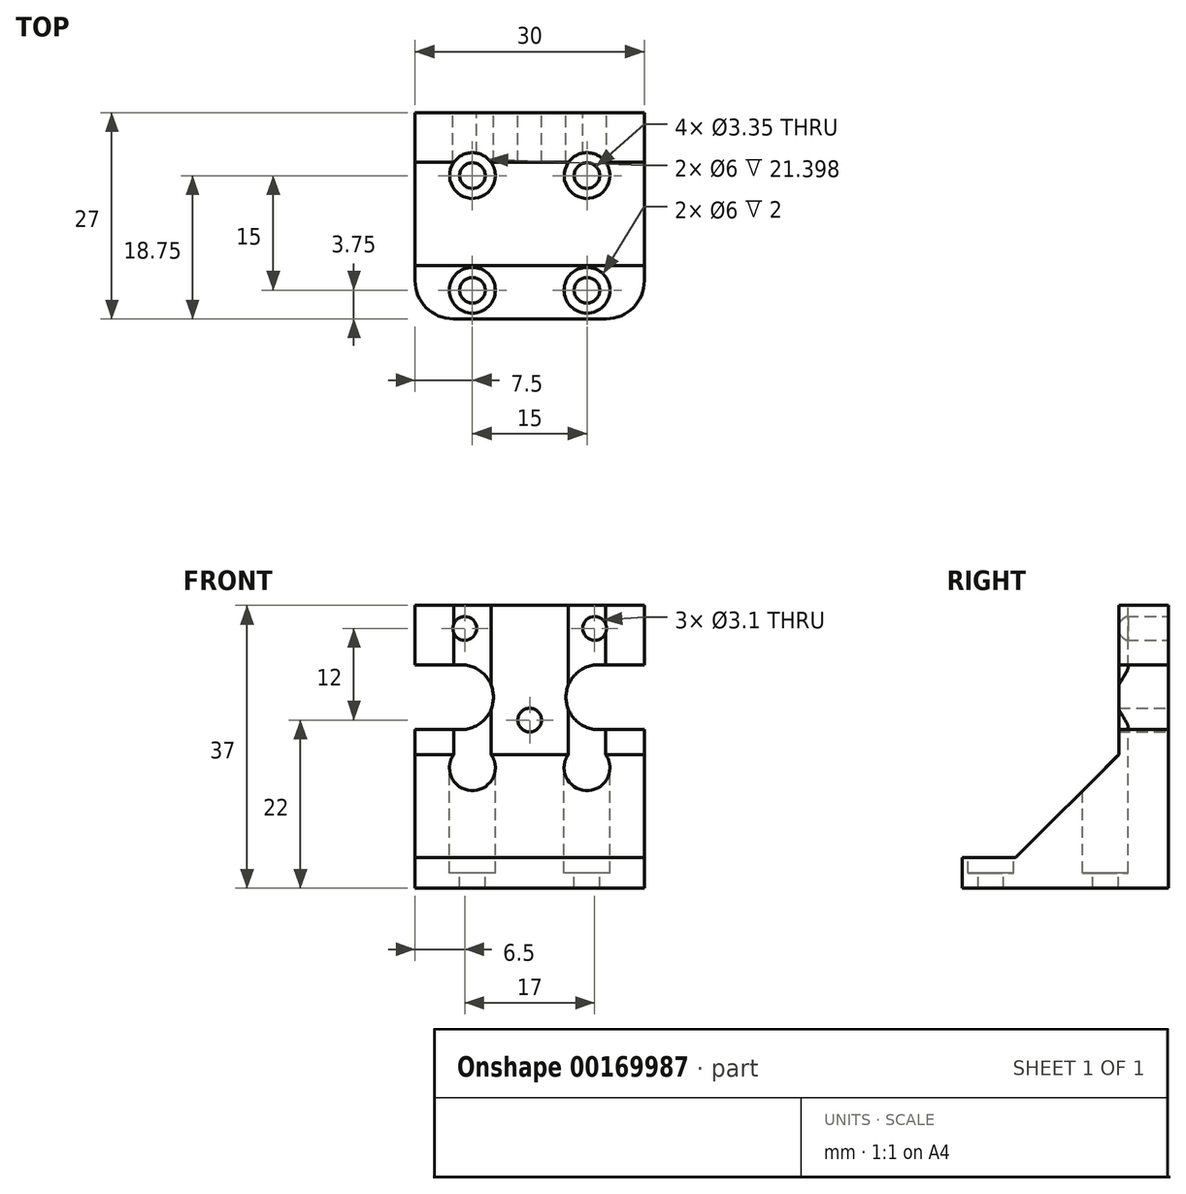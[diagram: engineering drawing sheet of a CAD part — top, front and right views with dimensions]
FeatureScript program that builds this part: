
annotation { "Feature Type Name" : "Feature", "Feature Type Description" : "" }
export const myFeature = defineFeature(function(context is Context, id is Id, definition is map)
    precondition{}
    {
        {
            var Q0;
            Q0=qCreatedBy(makeId("Top.planeOp"),FACE);
            var sketch = newSketch(context, id + "F0", { "sketchPlane" : qUnion([Q0])});
            skLineSegment(sketch, "E0.bottom", {"start": v(0, 0) * mm, "end": v(30, 0) * mm});
            skLineSegment(sketch, "E0.top", {"start": v(0, 22.5) * mm, "end": v(30, 22.5) * mm});
            skLineSegment(sketch, "E0.left", {"start": v(0, 0) * mm, "end": v(0, 22.5) * mm});
            skLineSegment(sketch, "E0.right", {"start": v(30, 0) * mm, "end": v(30, 22.5) * mm});
            skLineSegment(sketch, "E1.bottom", {"start": v(0, 27) * mm, "end": v(30, 27) * mm});
            skLineSegment(sketch, "E1.top", {"start": v(0, 20.5) * mm, "end": v(30, 20.5) * mm});
            skLineSegment(sketch, "E1.left", {"start": v(0, 27) * mm, "end": v(0, 20.5) * mm});
            skLineSegment(sketch, "E1.right", {"start": v(30, 27) * mm, "end": v(30, 20.5) * mm});
            skSolve(sketch);
        }
        {
            var Q0;
            Q0=makeQuery(id+"F0.imprint","IMPRINT",FACE,{"disambiguationData":[TD([[makeQuery(id+"F0.imprint","IMPRINT",EDGE,{"derivedFrom":sQuery(id+"F0.wireOp",EDGE,"E0.bottom")}),1.0]])]});
            var Q1;
            {var subQ0=sQuery(id+"F0.wireOp",EDGE,"E0.top");Q1=makeQuery(id+"F0.imprint","IMPRINT",FACE,{"disambiguationData":[TD([[makeQuery(id+"F0.imprint","IMPRINT",EDGE,{"derivedFrom":subQ0}),-1.0]])]});}
            extrude(context, id + "F1", {"entities" : qUnion([Q0, Q1]), "depth" : 4 * mm});
        }
        {
            var Q0;
            Q0=makeQuery(id+"F0.imprint","IMPRINT",FACE,{"disambiguationData":[TD([[makeQuery(id+"F0.imprint","IMPRINT",EDGE,{"derivedFrom":sQuery(id+"F0.wireOp",EDGE,"E0.top")}),1.0]])]});
            var Q1;
            {var subQ0=sQuery(id+"F0.wireOp",EDGE,"E0.top");Q1=makeQuery(id+"F0.imprint","IMPRINT",FACE,{"disambiguationData":[TD([[makeQuery(id+"F0.imprint","IMPRINT",EDGE,{"derivedFrom":subQ0}),-1.0]])]});}
            extrude(context, id + "F2", {"entities" : qUnion([Q0, Q1]), "operationType" : NewBodyOperationType.ADD, "depth" : 37 * mm});
        }
        {
            var Q0;
            Q0=makeQuery(id+"F1.opExtrude","CAP_FACE",FACE,{"disambiguationData":[OSD([sQuery(id+"F0.wireOp",EDGE,"E0.bottom"),sQuery(id+"F0.wireOp",EDGE,"E0.top"),sQuery(id+"F0.wireOp",EDGE,"E0.left"),sQuery(id+"F0.wireOp",EDGE,"E0.right")])],"isStart":false});
            var sketch = newSketch(context, id + "F3", { "sketchPlane" : qUnion([Q0])});
            skCircle(sketch, "E2", {"center": v(7.5, 18.75) * mm, "radius": 1.68 * mm});
            skCircle(sketch, "E3", {"center": v(22.5, 18.75) * mm, "radius": 1.68 * mm});
            skCircle(sketch, "E4", {"center": v(7.5, 3.75) * mm, "radius": 1.68 * mm});
            skCircle(sketch, "E5", {"center": v(22.5, 3.75) * mm, "radius": 1.68 * mm});
            skLineSegment(sketch, "E6", {"start": v(22.5, 3.75) * mm, "end": v(30, 3.75) * mm});
            skCircle(sketch, "E7", {"center": v(7.5, 18.75) * mm, "radius": 3 * mm});
            skCircle(sketch, "E8", {"center": v(22.5, 18.75) * mm, "radius": 3 * mm});
            skCircle(sketch, "E9", {"center": v(7.5, 3.75) * mm, "radius": 3 * mm});
            skCircle(sketch, "E10", {"center": v(22.5, 3.75) * mm, "radius": 3 * mm});
            skSolve(sketch);
        }
        {
            var Q0;
            Q0=makeQuery(id+"F3.imprint","IMPRINT",FACE,{"disambiguationData":[TD([[makeQuery(id+"F3.imprint","IMPRINT",EDGE,{"derivedFrom":sQuery(id+"F3.wireOp",EDGE,"E2")}),1.0]])]});
            var Q1;
            Q1=makeQuery(id+"F3.imprint","IMPRINT",FACE,{"disambiguationData":[TD([[makeQuery(id+"F3.imprint","IMPRINT",EDGE,{"derivedFrom":sQuery(id+"F3.wireOp",EDGE,"E3")}),1.0]])]});
            var Q2;
            Q2=makeQuery(id+"F3.imprint","IMPRINT",FACE,{"disambiguationData":[TD([[makeQuery(id+"F3.imprint","IMPRINT",EDGE,{"derivedFrom":sQuery(id+"F3.wireOp",EDGE,"E5")}),1.0]])]});
            var Q3;
            Q3=makeQuery(id+"F3.imprint","IMPRINT",FACE,{"disambiguationData":[TD([[makeQuery(id+"F3.imprint","IMPRINT",EDGE,{"derivedFrom":sQuery(id+"F3.wireOp",EDGE,"E4")}),1.0]])]});
            extrude(context, id + "F4", {"entities" : qUnion([Q0, Q1, Q2, Q3]), "operationType" : NewBodyOperationType.REMOVE, "oppositeDirection" : true, "depth" : 25 * mm});
        }
        {
            var Q0;
            Q0=makeQuery(id+"F3.imprint","IMPRINT",FACE,{"disambiguationData":[TD([[makeQuery(id+"F3.imprint","IMPRINT",EDGE,{"derivedFrom":sQuery(id+"F3.wireOp",EDGE,"E2")}),-1.0]])]});
            var Q1;
            Q1=makeQuery(id+"F3.imprint","IMPRINT",FACE,{"disambiguationData":[TD([[makeQuery(id+"F3.imprint","IMPRINT",EDGE,{"derivedFrom":sQuery(id+"F3.wireOp",EDGE,"E3")}),-1.0]])]});
            var Q2;
            Q2=makeQuery(id+"F3.imprint","IMPRINT",FACE,{"disambiguationData":[TD([[makeQuery(id+"F3.imprint","IMPRINT",EDGE,{"derivedFrom":sQuery(id+"F3.wireOp",EDGE,"E5")}),-1.0]])]});
            var Q3;
            Q3=makeQuery(id+"F3.imprint","IMPRINT",FACE,{"disambiguationData":[TD([[makeQuery(id+"F3.imprint","IMPRINT",EDGE,{"derivedFrom":sQuery(id+"F3.wireOp",EDGE,"E4")}),-1.0]])]});
            var Q4;
            {var subQ0=sQuery(id+"F3.wireOp",EDGE,"E7");var subQ1=makeQuery(id+"F2.boolean.opBoolean","INTERSECT",EDGE,{"derivedFrom":[makeQuery(id+"F1.opExtrude","CAP_FACE",FACE,{"disambiguationData":[OSD([sQuery(id+"F0.wireOp",EDGE,"E0.bottom"),sQuery(id+"F0.wireOp",EDGE,"E0.left"),sQuery(id+"F0.wireOp",EDGE,"E0.right"),sQuery(id+"F0.wireOp",EDGE,"E0.top"),sQuery(id+"F0.wireOp",EDGE,"E1.left"),sQuery(id+"F0.wireOp",EDGE,"E1.right")])],"isStart":false}),makeQuery(id+"F2.opExtrude","SWEPT_FACE",FACE,{"disambiguationData":[OSD([sQuery(id+"F0.wireOp",EDGE,"E1.top")])]})]});var subQ2=makeQuery(id+"F3.imprint","INTERSECT",VERTEX,{"disambiguationData":[OD(0.0)],"derivedFrom":[subQ1,subQ0]});Q4=makeQuery(id+"F3.imprint","IMPRINT",FACE,{"disambiguationData":[TD([[makeQuery(id+"F3.imprint","IMPRINT",EDGE,{"disambiguationData":[TD([[subQ2,1.0]])],"derivedFrom":subQ0}),1.0]])]});}
            var Q5;
            {var subQ0=sQuery(id+"F3.wireOp",EDGE,"E8");var subQ1=makeQuery(id+"F2.boolean.opBoolean","INTERSECT",EDGE,{"derivedFrom":[makeQuery(id+"F1.opExtrude","CAP_FACE",FACE,{"disambiguationData":[OSD([sQuery(id+"F0.wireOp",EDGE,"E0.bottom"),sQuery(id+"F0.wireOp",EDGE,"E0.left"),sQuery(id+"F0.wireOp",EDGE,"E0.right"),sQuery(id+"F0.wireOp",EDGE,"E0.top"),sQuery(id+"F0.wireOp",EDGE,"E1.left"),sQuery(id+"F0.wireOp",EDGE,"E1.right")])],"isStart":false}),makeQuery(id+"F2.opExtrude","SWEPT_FACE",FACE,{"disambiguationData":[OSD([sQuery(id+"F0.wireOp",EDGE,"E1.top")])]})]});var subQ2=makeQuery(id+"F3.imprint","INTERSECT",VERTEX,{"disambiguationData":[OD(0.0)],"derivedFrom":[subQ1,subQ0]});Q5=makeQuery(id+"F3.imprint","IMPRINT",FACE,{"disambiguationData":[TD([[makeQuery(id+"F3.imprint","IMPRINT",EDGE,{"disambiguationData":[TD([[subQ2,-1.0]])],"derivedFrom":subQ0}),1.0]])]});}
            extrude(context, id + "F5", {"entities" : qUnion([Q0, Q1, Q2, Q3, Q4, Q5]), "operationType" : NewBodyOperationType.REMOVE, "oppositeDirection" : true, "depth" : 2 * mm});
        }
        {
            var Q0;
            {var subQ0=sQuery(id+"F3.wireOp",EDGE,"E7");var subQ1=makeQuery(id+"F2.boolean.opBoolean","INTERSECT",EDGE,{"derivedFrom":[makeQuery(id+"F1.opExtrude","CAP_FACE",FACE,{"disambiguationData":[OSD([sQuery(id+"F0.wireOp",EDGE,"E0.bottom"),sQuery(id+"F0.wireOp",EDGE,"E0.left"),sQuery(id+"F0.wireOp",EDGE,"E0.right"),sQuery(id+"F0.wireOp",EDGE,"E0.top"),sQuery(id+"F0.wireOp",EDGE,"E1.left"),sQuery(id+"F0.wireOp",EDGE,"E1.right")])],"isStart":false}),makeQuery(id+"F2.opExtrude","SWEPT_FACE",FACE,{"disambiguationData":[OSD([sQuery(id+"F0.wireOp",EDGE,"E1.top")])]})]});var subQ2=makeQuery(id+"F3.imprint","INTERSECT",VERTEX,{"disambiguationData":[OD(0.0)],"derivedFrom":[subQ1,subQ0]});Q0=makeQuery(id+"F3.imprint","IMPRINT",FACE,{"disambiguationData":[TD([[makeQuery(id+"F3.imprint","IMPRINT",EDGE,{"disambiguationData":[TD([[subQ2,1.0]])],"derivedFrom":subQ0}),1.0]])]});}
            var Q1;
            Q1=makeQuery(id+"F3.imprint","IMPRINT",FACE,{"disambiguationData":[TD([[makeQuery(id+"F3.imprint","IMPRINT",EDGE,{"derivedFrom":sQuery(id+"F3.wireOp",EDGE,"E2")}),-1.0]])]});
            var Q2;
            {var subQ0=sQuery(id+"F3.wireOp",EDGE,"E8");var subQ1=makeQuery(id+"F2.boolean.opBoolean","INTERSECT",EDGE,{"derivedFrom":[makeQuery(id+"F1.opExtrude","CAP_FACE",FACE,{"disambiguationData":[OSD([sQuery(id+"F0.wireOp",EDGE,"E0.bottom"),sQuery(id+"F0.wireOp",EDGE,"E0.left"),sQuery(id+"F0.wireOp",EDGE,"E0.right"),sQuery(id+"F0.wireOp",EDGE,"E0.top"),sQuery(id+"F0.wireOp",EDGE,"E1.left"),sQuery(id+"F0.wireOp",EDGE,"E1.right")])],"isStart":false}),makeQuery(id+"F2.opExtrude","SWEPT_FACE",FACE,{"disambiguationData":[OSD([sQuery(id+"F0.wireOp",EDGE,"E1.top")])]})]});var subQ2=makeQuery(id+"F3.imprint","INTERSECT",VERTEX,{"disambiguationData":[OD(0.0)],"derivedFrom":[subQ1,subQ0]});Q2=makeQuery(id+"F3.imprint","IMPRINT",FACE,{"disambiguationData":[TD([[makeQuery(id+"F3.imprint","IMPRINT",EDGE,{"disambiguationData":[TD([[subQ2,-1.0]])],"derivedFrom":subQ0}),1.0]])]});}
            var Q3;
            Q3=makeQuery(id+"F3.imprint","IMPRINT",FACE,{"disambiguationData":[TD([[makeQuery(id+"F3.imprint","IMPRINT",EDGE,{"derivedFrom":sQuery(id+"F3.wireOp",EDGE,"E3")}),-1.0]])]});
            var Q4;
            Q4=makeQuery(id+"F2.opExtrude","CAP_FACE",FACE,{"disambiguationData":[OSD([sQuery(id+"F0.wireOp",EDGE,"E1.bottom"),sQuery(id+"F0.wireOp",EDGE,"E1.top"),sQuery(id+"F0.wireOp",EDGE,"E1.left"),sQuery(id+"F0.wireOp",EDGE,"E1.right")])],"isStart":false});
            extrude(context, id + "F6", {"entities" : qUnion([Q0, Q1, Q2, Q3]), "operationType" : NewBodyOperationType.REMOVE, "endBound" : BoundingType.UP_TO_SURFACE, "endBoundEntityFace" : qUnion([Q4]), "depth" : 25 * mm});
        }
        {
            var Q0;
            Q0=makeQuery(id+"F1.opExtrude","SWEPT_EDGE",EDGE,{"disambiguationData":[OSD([sQuery(id+"F0.wireOp",EDGE,"E0.bottom"),sQuery(id+"F0.wireOp",EDGE,"E0.left")])]});
            var Q1;
            Q1=makeQuery(id+"F1.opExtrude","SWEPT_EDGE",EDGE,{"disambiguationData":[OSD([sQuery(id+"F0.wireOp",EDGE,"E0.bottom"),sQuery(id+"F0.wireOp",EDGE,"E0.right")])]});
            var Q2;
            Q2=makeQuery(id+"F1.opExtrude","SWEPT_EDGE",EDGE,{"disambiguationData":[OSD([sQuery(id+"F0.wireOp",EDGE,"E0.top"),sQuery(id+"F0.wireOp",EDGE,"E0.right")])]});
            var Q3;
            Q3=makeQuery(id+"F1.opExtrude","SWEPT_EDGE",EDGE,{"disambiguationData":[OSD([sQuery(id+"F0.wireOp",EDGE,"E0.top"),sQuery(id+"F0.wireOp",EDGE,"E0.left")])]});
            fillet(context, id + "F7", {"entities" : qUnion([Q0, Q1, Q2, Q3]), "radius" : 5 * mm, "tangentPropagation" : true, "allowEdgeOverflow" : false});
        }
        {
            var Q0;
            Q0=makeQuery(id+"F2.opExtrude","SWEPT_FACE",FACE,{"disambiguationData":[OSD([sQuery(id+"F0.wireOp",EDGE,"E1.bottom")])]});
            var sketch = newSketch(context, id + "F8", { "sketchPlane" : qUnion([Q0])});
            skCircle(sketch, "E11", {"center": v(-23.5, 34) * mm, "radius": 1.55 * mm});
            skCircle(sketch, "E12", {"center": v(-6.5, 34) * mm, "radius": 1.55 * mm});
            skCircle(sketch, "E13", {"center": v(-15, 22) * mm, "radius": 1.55 * mm});
            skCircle(sketch, "E14", {"center": v(-24, 25) * mm, "radius": 4.25 * mm});
            skCircle(sketch, "E15", {"center": v(-6, 25) * mm, "radius": 4.25 * mm});
            skSolve(sketch);
        }
        {
            var Q0;
            Q0=makeQuery(id+"F8.imprint","IMPRINT",FACE,{"disambiguationData":[TD([[makeQuery(id+"F8.imprint","IMPRINT",EDGE,{"derivedFrom":sQuery(id+"F8.wireOp",EDGE,"E14")}),1.0]])]});
            var Q1;
            Q1=makeQuery(id+"F8.imprint","IMPRINT",FACE,{"disambiguationData":[TD([[makeQuery(id+"F8.imprint","IMPRINT",EDGE,{"derivedFrom":sQuery(id+"F8.wireOp",EDGE,"E11")}),1.0]])]});
            var Q2;
            Q2=makeQuery(id+"F8.imprint","IMPRINT",FACE,{"disambiguationData":[TD([[makeQuery(id+"F8.imprint","IMPRINT",EDGE,{"derivedFrom":sQuery(id+"F8.wireOp",EDGE,"E12")}),1.0]])]});
            var Q3;
            Q3=makeQuery(id+"F8.imprint","IMPRINT",FACE,{"disambiguationData":[TD([[makeQuery(id+"F8.imprint","IMPRINT",EDGE,{"derivedFrom":sQuery(id+"F8.wireOp",EDGE,"E15")}),1.0]])]});
            var Q4;
            Q4=makeQuery(id+"F8.imprint","IMPRINT",FACE,{"disambiguationData":[TD([[makeQuery(id+"F8.imprint","IMPRINT",EDGE,{"derivedFrom":sQuery(id+"F8.wireOp",EDGE,"E13")}),1.0]])]});
            extrude(context, id + "F9", {"entities" : qUnion([Q0, Q1, Q2, Q3, Q4]), "operationType" : NewBodyOperationType.REMOVE, "oppositeDirection" : true, "depth" : 7 * mm});
        }
        {
            var Q0;
            {var subQ0=sQuery(id+"F0.wireOp",EDGE,"E1.left");var subQ1=sQuery(id+"F3.wireOp",EDGE,"E7");var subQ2=makeQuery(id+"F2.opExtrude","SWEPT_FACE",FACE,{"disambiguationData":[OSD([sQuery(id+"F0.wireOp",EDGE,"E1.top")])]});var subQ3=sQuery(id+"F0.wireOp",EDGE,"E0.left");var subQ4=makeQuery(id+"F1.opExtrude","CAP_FACE",FACE,{"disambiguationData":[OSD([sQuery(id+"F0.wireOp",EDGE,"E0.bottom"),subQ3,sQuery(id+"F0.wireOp",EDGE,"E0.right"),sQuery(id+"F0.wireOp",EDGE,"E0.top"),subQ0,sQuery(id+"F0.wireOp",EDGE,"E1.right")])],"isStart":false});Q0=makeQuery(id+"F5.boolean.opBoolean","SPLIT",EDGE,{"disambiguationData":[TD([subQ4,makeQuery(id+"F1.opExtrude","SWEPT_FACE",FACE,{"disambiguationData":[OSD([subQ3,subQ0])]}),subQ2,makeQuery(id+"F2.opExtrude","SWEPT_FACE",FACE,{"disambiguationData":[OSD([subQ0])]}),makeQuery(id+"F5.opExtrude","CAP_FACE",FACE,{"disambiguationData":[OSD([sQuery(id+"F3.wireOp",EDGE,"E2"),subQ1])],"isStart":true}),makeQuery(id+"F5.opExtrude","SWEPT_FACE",FACE,{"disambiguationData":[OSD([subQ1])]})])],"derivedFrom":makeQuery(id+"F2.boolean.opBoolean","INTERSECT",EDGE,{"derivedFrom":[subQ4,subQ2]})});}
            var Q1;
            {var subQ0=sQuery(id+"F3.wireOp",EDGE,"E8");var subQ1=sQuery(id+"F3.wireOp",EDGE,"E7");var subQ2=makeQuery(id+"F2.opExtrude","SWEPT_FACE",FACE,{"disambiguationData":[OSD([sQuery(id+"F0.wireOp",EDGE,"E1.top")])]});var subQ3=makeQuery(id+"F1.opExtrude","CAP_FACE",FACE,{"disambiguationData":[OSD([sQuery(id+"F0.wireOp",EDGE,"E0.bottom"),sQuery(id+"F0.wireOp",EDGE,"E0.left"),sQuery(id+"F0.wireOp",EDGE,"E0.right"),sQuery(id+"F0.wireOp",EDGE,"E0.top"),sQuery(id+"F0.wireOp",EDGE,"E1.left"),sQuery(id+"F0.wireOp",EDGE,"E1.right")])],"isStart":false});Q1=makeQuery(id+"F5.boolean.opBoolean","SPLIT",EDGE,{"disambiguationData":[TD([subQ3,subQ2,makeQuery(id+"F5.opExtrude","CAP_FACE",FACE,{"disambiguationData":[OSD([sQuery(id+"F3.wireOp",EDGE,"E2"),subQ1])],"isStart":true}),makeQuery(id+"F5.opExtrude","CAP_FACE",FACE,{"disambiguationData":[OSD([sQuery(id+"F3.wireOp",EDGE,"E3"),subQ0])],"isStart":true}),makeQuery(id+"F5.opExtrude","SWEPT_FACE",FACE,{"disambiguationData":[OSD([subQ1])]}),makeQuery(id+"F5.opExtrude","SWEPT_FACE",FACE,{"disambiguationData":[OSD([subQ0])]})])],"derivedFrom":makeQuery(id+"F2.boolean.opBoolean","INTERSECT",EDGE,{"derivedFrom":[subQ3,subQ2]})});}
            var Q2;
            {var subQ0=sQuery(id+"F0.wireOp",EDGE,"E1.right");var subQ1=sQuery(id+"F3.wireOp",EDGE,"E8");var subQ2=makeQuery(id+"F2.opExtrude","SWEPT_FACE",FACE,{"disambiguationData":[OSD([sQuery(id+"F0.wireOp",EDGE,"E1.top")])]});var subQ3=sQuery(id+"F0.wireOp",EDGE,"E0.right");var subQ4=makeQuery(id+"F1.opExtrude","CAP_FACE",FACE,{"disambiguationData":[OSD([sQuery(id+"F0.wireOp",EDGE,"E0.bottom"),sQuery(id+"F0.wireOp",EDGE,"E0.left"),subQ3,sQuery(id+"F0.wireOp",EDGE,"E0.top"),sQuery(id+"F0.wireOp",EDGE,"E1.left"),subQ0])],"isStart":false});Q2=makeQuery(id+"F5.boolean.opBoolean","SPLIT",EDGE,{"disambiguationData":[TD([subQ4,makeQuery(id+"F1.opExtrude","SWEPT_FACE",FACE,{"disambiguationData":[OSD([subQ3,subQ0])]}),subQ2,makeQuery(id+"F2.opExtrude","SWEPT_FACE",FACE,{"disambiguationData":[OSD([subQ0])]}),makeQuery(id+"F5.opExtrude","CAP_FACE",FACE,{"disambiguationData":[OSD([sQuery(id+"F3.wireOp",EDGE,"E3"),subQ1])],"isStart":true}),makeQuery(id+"F5.opExtrude","SWEPT_FACE",FACE,{"disambiguationData":[OSD([subQ1])]})])],"derivedFrom":makeQuery(id+"F2.boolean.opBoolean","INTERSECT",EDGE,{"derivedFrom":[subQ4,subQ2]})});}
            chamfer(context, id + "F10", {"entities" : qUnion([Q0, Q1, Q2]), "width" : 13.5 * mm, "tangentPropagation" : true});
        }
        {
            var Q0;
            Q0=makeQuery(id+"F2.opExtrude","SWEPT_FACE",FACE,{"disambiguationData":[OSD([sQuery(id+"F0.wireOp",EDGE,"E1.bottom")])]});
            var sketch = newSketch(context, id + "F11", { "sketchPlane" : qUnion([Q0])});
            skLineSegment(sketch, "E16", {"start": v(-6, 25) * mm, "end": v(-6, 29.25) * mm});
            skLineSegment(sketch, "E17", {"start": v(-6, 29.25) * mm, "end": v(0, 29.25) * mm});
            skLineSegment(sketch, "E18", {"start": v(-6, 25) * mm, "end": v(-6, 20.75) * mm});
            skLineSegment(sketch, "E19", {"start": v(-6, 20.75) * mm, "end": v(0, 20.75) * mm});
            skLineSegment(sketch, "E20", {"start": v(0, 20.75) * mm, "end": v(0, 29.25) * mm});
            skLineSegment(sketch, "E21", {"start": v(-15, 37) * mm, "end": v(-15, 10.06) * mm});
            skLineSegment(sketch, "E22.MirrorCS", {"start": v(-24, 29.25) * mm, "end": v(-30, 29.25) * mm});
            skLineSegment(sketch, "E23.MirrorCS", {"start": v(-30, 20.75) * mm, "end": v(-30, 29.25) * mm});
            skLineSegment(sketch, "E24.MirrorCS", {"start": v(-24, 20.75) * mm, "end": v(-30, 20.75) * mm});
            skLineSegment(sketch, "E25.MirrorCS", {"start": v(-24, 25) * mm, "end": v(-24, 20.75) * mm});
            skLineSegment(sketch, "E26.MirrorCS", {"start": v(-24, 25) * mm, "end": v(-24, 29.25) * mm});
            skSolve(sketch);
        }
        {
            var Q0;
            {var subQ0=sQuery(id+"F11.wireOp",EDGE,"E17");Q0=makeQuery(id+"F11.imprint","IMPRINT",FACE,{"disambiguationData":[TD([[makeQuery(id+"F11.imprint","IMPRINT",EDGE,{"derivedFrom":subQ0}),-1.0]])]});}
            var Q1;
            {var subQ0=sQuery(id+"F11.wireOp",EDGE,"E22.MirrorCS");Q1=makeQuery(id+"F11.imprint","IMPRINT",FACE,{"disambiguationData":[TD([[makeQuery(id+"F11.imprint","IMPRINT",EDGE,{"derivedFrom":subQ0}),1.0]])]});}
            extrude(context, id + "F12", {"entities" : qUnion([Q0, Q1]), "operationType" : NewBodyOperationType.REMOVE, "endBound" : BoundingType.UP_TO_NEXT, "oppositeDirection" : true, "depth" : 25 * mm});
        }
    });
